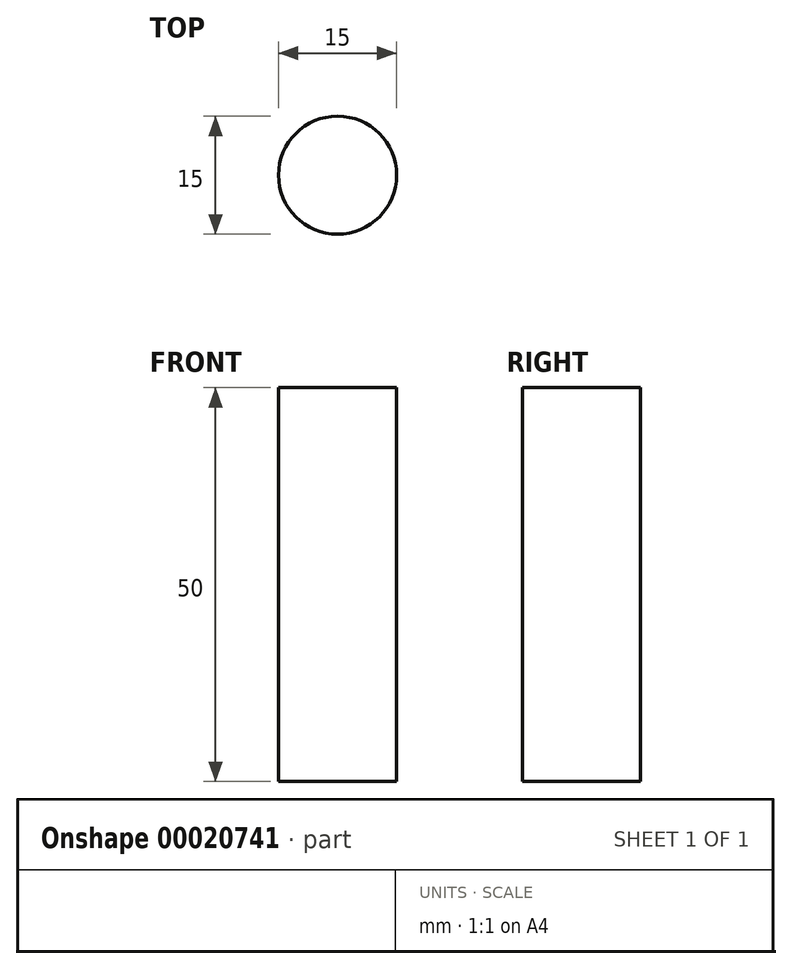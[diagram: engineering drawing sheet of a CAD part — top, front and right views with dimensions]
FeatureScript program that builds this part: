
annotation { "Feature Type Name" : "Feature", "Feature Type Description" : "" }
export const myFeature = defineFeature(function(context is Context, id is Id, definition is map)
    precondition{}
    {
        {
            var Q0;
            Q0=qCreatedBy(makeId("Top.planeOp"),FACE);
            var sketch = newSketch(context, id + "F0", { "sketchPlane" : qUnion([Q0])});
            skCircle(sketch, "E0", {"center": v(0, 0) * mm, "radius": 7.5 * mm});
            skSolve(sketch);
        }
        {
            var Q0;
            Q0 = qSketchRegion(id + "F0", true);
            extrude(context, id + "F1", {"entities" : qUnion([Q0]), "depth" : 50 * mm});
        }
    });
